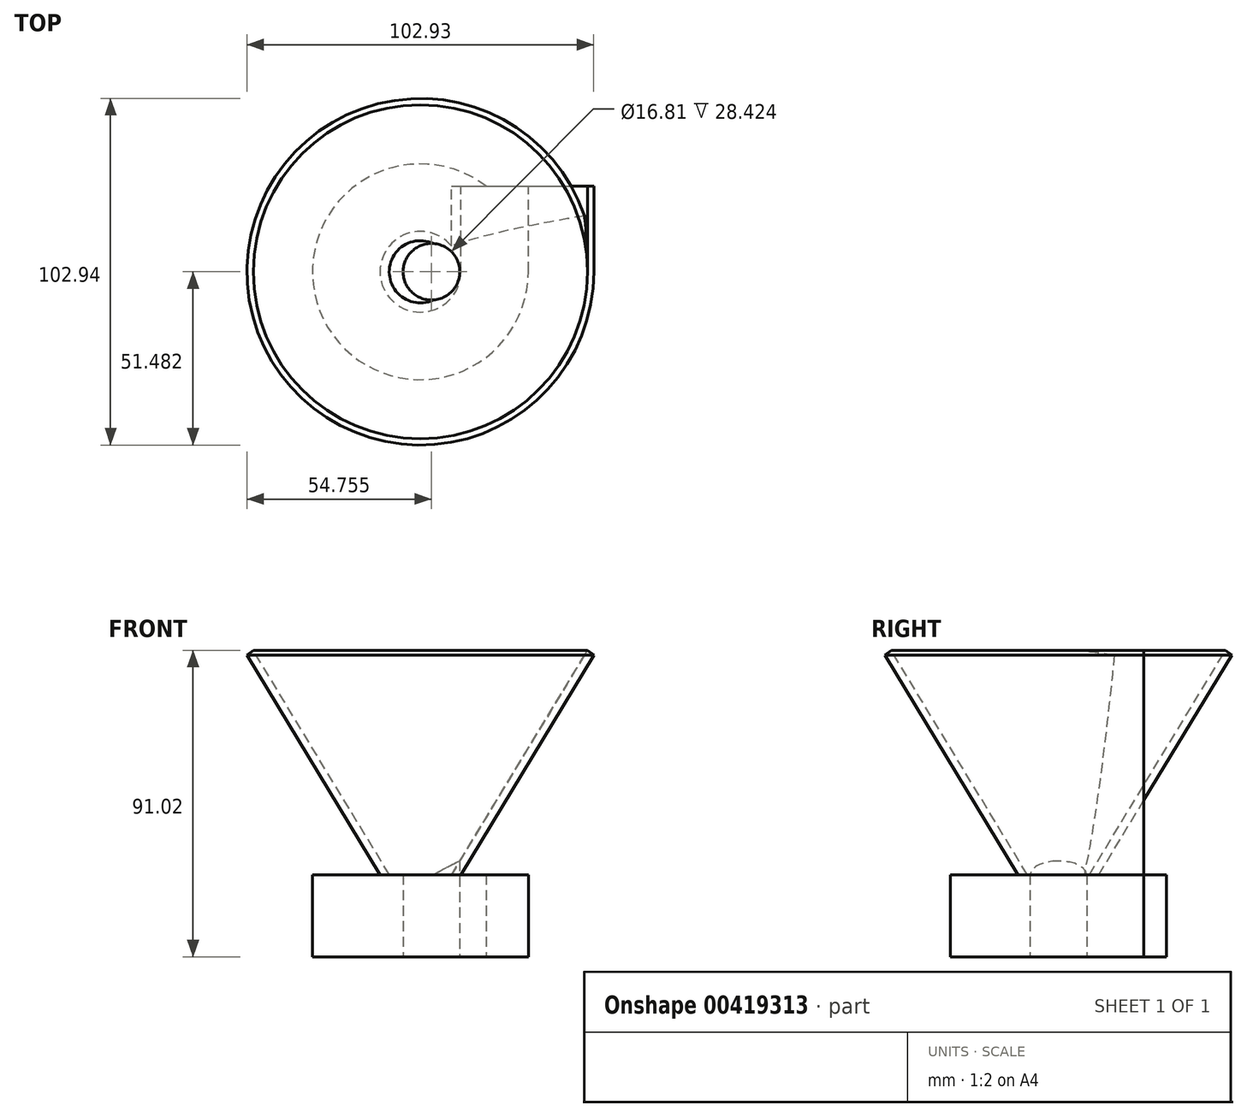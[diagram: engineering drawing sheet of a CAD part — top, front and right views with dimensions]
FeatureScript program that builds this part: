
annotation { "Feature Type Name" : "Feature", "Feature Type Description" : "" }
export const myFeature = defineFeature(function(context is Context, id is Id, definition is map)
    precondition{}
    {
        {
            var Q0;
            Q0=qCreatedBy(makeId("Front.planeOp"),FACE);
            var sketch = newSketch(context, id + "F0", { "sketchPlane" : qUnion([Q0])});
            skLineSegment(sketch, "E0", {"start": v(0, 0) * mm, "end": v(26.32, 43.45) * mm});
            skLineSegment(sketch, "E1", {"start": v(26.32, 43.45) * mm, "end": v(39.47, 65.18) * mm});
            skLineSegment(sketch, "E2", {"start": v(0, 0) * mm, "end": v(20.05, 0) * mm});
            skLineSegment(sketch, "E3", {"start": v(20.05, 0) * mm, "end": v(20.05, -24.38) * mm});
            skLineSegment(sketch, "E4", {"start": v(20.05, -24.38) * mm, "end": v(-12, -24.38) * mm});
            skLineSegment(sketch, "E5", {"start": v(-12, -24.38) * mm, "end": v(-12, 0) * mm});
            skLineSegment(sketch, "E6", {"start": v(-12, 0) * mm, "end": v(-2.75, 0) * mm});
            skLineSegment(sketch, "E7", {"start": v(-2.75, 0) * mm, "end": v(37.6, 66.64) * mm});
            skLineSegment(sketch, "E8", {"start": v(37.6, 66.64) * mm, "end": v(39.47, 65.18) * mm});
            skSolve(sketch);
        }
        {
            var Q0;
            Q0 = qSketchRegion(id + "F0", true);
            extrude(context, id + "F1", {"entities" : qUnion([Q0]), "depth" : 25.4 * mm});
        }
        {
            var Q0;
            Q0=makeQuery(id+"F1.opExtrude","CAP_FACE",FACE,{"disambiguationData":[OSD([sQuery(id+"F0.wireOp",EDGE,"E0"),sQuery(id+"F0.wireOp",EDGE,"E1"),sQuery(id+"F0.wireOp",EDGE,"E2"),sQuery(id+"F0.wireOp",EDGE,"E3"),sQuery(id+"F0.wireOp",EDGE,"E4"),sQuery(id+"F0.wireOp",EDGE,"E5"),sQuery(id+"F0.wireOp",EDGE,"E6"),sQuery(id+"F0.wireOp",EDGE,"E7"),sQuery(id+"F0.wireOp",EDGE,"E8")])],"isStart":false});
            var Q1;
            Q1=makeQuery(id+"F1.opExtrude","CAP_EDGE",EDGE,{"disambiguationData":[OSD([sQuery(id+"F0.wireOp",EDGE,"E5")])],"isStart":false});
            revolve(context, id + "F2", {"operationType" : NewBodyOperationType.ADD, "entities" : qUnion([Q0]), "axis" : qUnion([Q1]), "revolveType" : RevolveType.FULL});
        }
        {
            var Q0;
            {var subQ0=sQuery(id+"F0.wireOp",EDGE,"E4");Q0=makeQuery(id+"F2.boolean.opBoolean","MERGE",FACE,{"derivedFrom":[makeQuery(id+"F1.opExtrude","SWEPT_FACE",FACE,{"disambiguationData":[OSD([subQ0])]}),makeQuery(id+"F2.opRevolve","SWEPT_FACE",FACE,{"disambiguationData":[OSD([subQ0])]})]});}
            var sketch = newSketch(context, id + "F3", { "sketchPlane" : qUnion([Q0])});
            skCircle(sketch, "E9", {"center": v(-8.7, 25.39) * mm, "radius": 8.4 * mm});
            skSolve(sketch);
        }
        {
            var Q0;
            Q0 = qSketchRegion(id + "F3", true);
            extrude(context, id + "F4", {"entities" : qUnion([Q0]), "operationType" : NewBodyOperationType.REMOVE, "oppositeDirection" : true, "depth" : 50.8 * mm});
        }
    });
